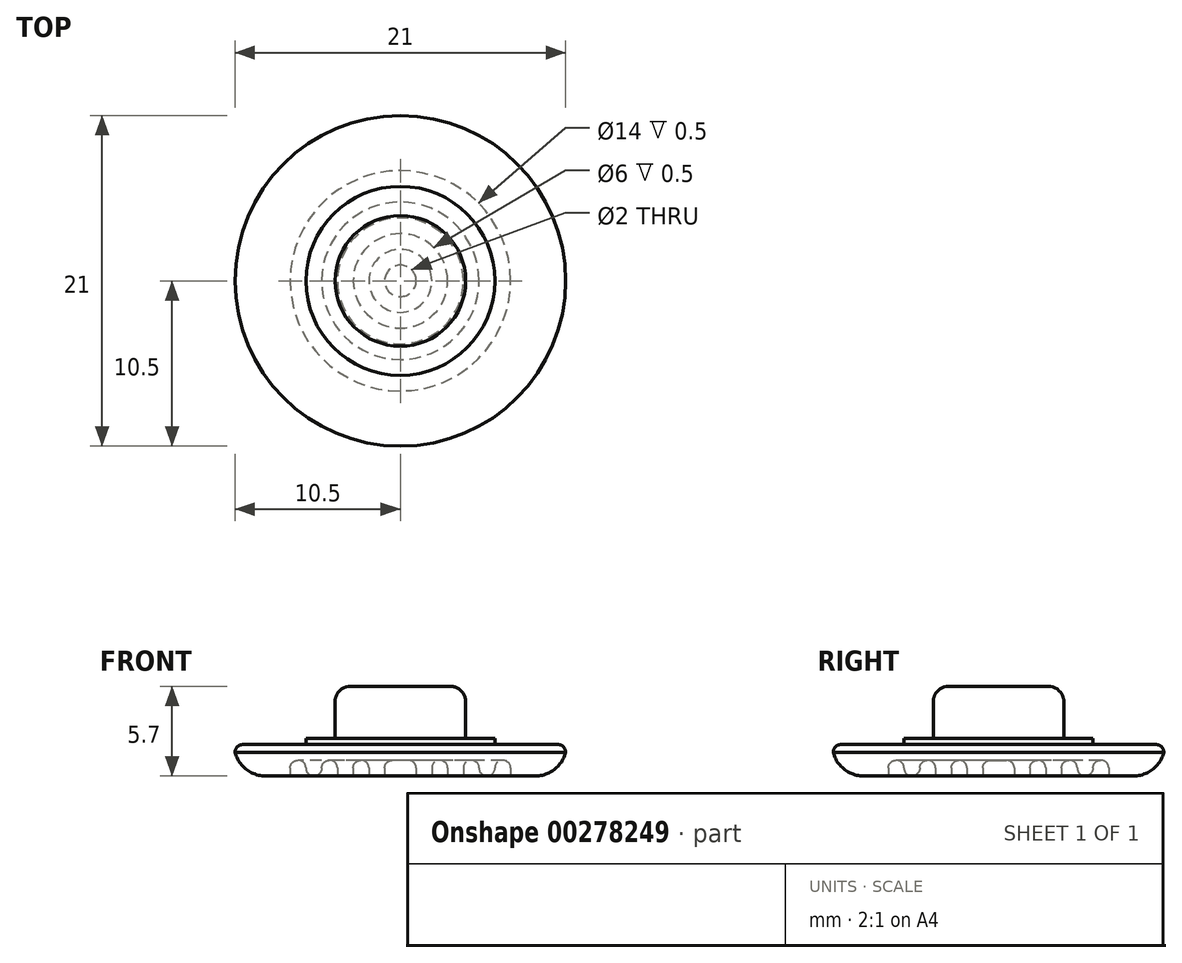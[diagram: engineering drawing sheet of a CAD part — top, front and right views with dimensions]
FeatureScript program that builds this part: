
annotation { "Feature Type Name" : "Feature", "Feature Type Description" : "" }
export const myFeature = defineFeature(function(context is Context, id is Id, definition is map)
    precondition{}
    {
        {
            var Q0;
            Q0=qCreatedBy(makeId("Top.planeOp"),FACE);
            var sketch = newSketch(context, id + "F0", { "sketchPlane" : qUnion([Q0])});
            skCircle(sketch, "E0", {"center": v(27.79, 0.83) * mm, "radius": 4.15 * mm});
            skCircle(sketch, "E1", {"center": v(27.79, 0.83) * mm, "radius": 11 * mm});
            skCircle(sketch, "E2", {"center": v(27.79, 0.83) * mm, "radius": 6 * mm});
            skCircle(sketch, "E3", {"center": v(0, 0) * mm, "radius": 4.15 * mm});
            skCircle(sketch, "E4", {"center": v(0, 0) * mm, "radius": 6 * mm});
            skCircle(sketch, "E5", {"center": v(0, 0) * mm, "radius": 10.5 * mm});
            skSolve(sketch);
        }
        {
            var Q0;
            Q0=makeQuery(id+"F0.imprint","IMPRINT",FACE,{"disambiguationData":[TD([[makeQuery(id+"F0.imprint","IMPRINT",EDGE,{"derivedFrom":sQuery(id+"F0.wireOp",EDGE,"E4")}),-1.0]])]});
            extrude(context, id + "F1", {"entities" : qUnion([Q0]), "depth" : 2 * mm, "offsetDistance" : 25 * mm});
        }
        {
            var Q0;
            Q0=makeQuery(id+"F0.imprint","IMPRINT",FACE,{"disambiguationData":[TD([[makeQuery(id+"F0.imprint","IMPRINT",EDGE,{"derivedFrom":sQuery(id+"F0.wireOp",EDGE,"E3")}),-1.0]])]});
            extrude(context, id + "F2", {"entities" : qUnion([Q0]), "operationType" : NewBodyOperationType.ADD, "depth" : 2.4 * mm, "offsetDistance" : 25 * mm});
        }
        {
            var Q0;
            Q0=makeQuery(id+"F0.imprint","IMPRINT",FACE,{"disambiguationData":[TD([[makeQuery(id+"F0.imprint","IMPRINT",EDGE,{"derivedFrom":sQuery(id+"F0.wireOp",EDGE,"E3")}),1.0]])]});
            extrude(context, id + "F3", {"entities" : qUnion([Q0]), "operationType" : NewBodyOperationType.ADD, "depth" : 5.7 * mm, "offsetDistance" : 25 * mm});
        }
        {
            var Q0;
            Q0=makeQuery(id+"F3.opExtrude","CAP_EDGE",EDGE,{"disambiguationData":[OSD([sQuery(id+"F0.wireOp",EDGE,"E3")])],"isStart":false});
            fillet(context, id + "F4", {"entities" : qUnion([Q0]), "radius" : 1 * mm, "tangentPropagation" : true, "allowEdgeOverflow" : false});
        }
        {
            var Q0;
            Q0=makeQuery(id+"F1.opExtrude","CAP_EDGE",EDGE,{"disambiguationData":[OSD([sQuery(id+"F0.wireOp",EDGE,"E5")])],"isStart":false});
            fillet(context, id + "F5", {"entities" : qUnion([Q0]), "radius" : .5 * mm, "tangentPropagation" : true, "allowEdgeOverflow" : false});
        }
        {
            var Q0;
            Q0=makeQuery(id+"F1.opExtrude","CAP_EDGE",EDGE,{"disambiguationData":[OSD([sQuery(id+"F0.wireOp",EDGE,"E5")])],"isStart":true});
            fillet(context, id + "F6", {"entities" : qUnion([Q0]), "radius" : 2 * mm, "tangentPropagation" : true, "allowEdgeOverflow" : false});
        }
        {
            var Q0;
            Q0=makeQuery(id+"F0.imprint","IMPRINT",FACE,{"disambiguationData":[TD([[makeQuery(id+"F0.imprint","IMPRINT",EDGE,{"derivedFrom":sQuery(id+"F0.wireOp",EDGE,"E3")}),1.0]])]});
            var sketch = newSketch(context, id + "F7", { "sketchPlane" : qUnion([Q0])});
            skCircle(sketch, "E6", {"center": v(0, 0) * mm, "radius": 11 * mm});
            skCircle(sketch, "E7", {"center": v(0, 0) * mm, "radius": 8 * mm});
            skCircle(sketch, "E8", {"center": v(0, 0) * mm, "radius": 7.5 * mm});
            skCircle(sketch, "E9", {"center": v(0, 0) * mm, "radius": 7 * mm});
            skCircle(sketch, "E10", {"center": v(0, 0) * mm, "radius": 6 * mm});
            skCircle(sketch, "E11", {"center": v(0, 0) * mm, "radius": 5.5 * mm});
            skCircle(sketch, "E12", {"center": v(0, 0) * mm, "radius": 5 * mm});
            skCircle(sketch, "E13", {"center": v(0, 0) * mm, "radius": 4.5 * mm});
            skCircle(sketch, "E14", {"center": v(0, 0) * mm, "radius": 4 * mm});
            skCircle(sketch, "E15", {"center": v(0, 0) * mm, "radius": 3.5 * mm});
            skCircle(sketch, "E16", {"center": v(0, 0) * mm, "radius": 3 * mm});
            skCircle(sketch, "E17", {"center": v(0, 0) * mm, "radius": 2.5 * mm});
            skCircle(sketch, "E18", {"center": v(0, 0) * mm, "radius": 2 * mm});
            skCircle(sketch, "E19", {"center": v(0, 0) * mm, "radius": 1.5 * mm});
            skCircle(sketch, "E20", {"center": v(0, 0) * mm, "radius": 1 * mm});
            skCircle(sketch, "E21", {"center": v(0, 0) * mm, "radius": 0.5 * mm});
            skCircle(sketch, "E22", {"center": v(0, 0) * mm, "radius": 6.5 * mm});
            skCircle(sketch, "E23", {"center": v(0, 0) * mm, "radius": 8.5 * mm});
            skCircle(sketch, "E24", {"center": v(0, 0) * mm, "radius": 9 * mm});
            skSolve(sketch);
        }
        {
            var Q0;
            Q0=makeQuery(id+"F7.imprint","IMPRINT",FACE,{"disambiguationData":[TD([[makeQuery(id+"F7.imprint","IMPRINT",EDGE,{"derivedFrom":sQuery(id+"F7.wireOp",EDGE,"E21")}),1.0]])]});
            var Q1;
            Q1=makeQuery(id+"F7.imprint","IMPRINT",FACE,{"disambiguationData":[TD([[makeQuery(id+"F7.imprint","IMPRINT",EDGE,{"derivedFrom":sQuery(id+"F7.wireOp",EDGE,"E20")}),1.0]])]});
            var Q2;
            Q2=makeQuery(id+"F7.imprint","IMPRINT",FACE,{"disambiguationData":[TD([[makeQuery(id+"F7.imprint","IMPRINT",EDGE,{"derivedFrom":sQuery(id+"F7.wireOp",EDGE,"E17")}),1.0]])]});
            var Q3;
            Q3=makeQuery(id+"F7.imprint","IMPRINT",FACE,{"disambiguationData":[TD([[makeQuery(id+"F7.imprint","IMPRINT",EDGE,{"derivedFrom":sQuery(id+"F7.wireOp",EDGE,"E16")}),1.0]])]});
            var Q4;
            Q4=makeQuery(id+"F7.imprint","IMPRINT",FACE,{"disambiguationData":[TD([[makeQuery(id+"F7.imprint","IMPRINT",EDGE,{"derivedFrom":sQuery(id+"F7.wireOp",EDGE,"E13")}),1.0]])]});
            var Q5;
            Q5=makeQuery(id+"F7.imprint","IMPRINT",FACE,{"disambiguationData":[TD([[makeQuery(id+"F7.imprint","IMPRINT",EDGE,{"derivedFrom":sQuery(id+"F7.wireOp",EDGE,"E14")}),-1.0]])]});
            var Q6;
            Q6=makeQuery(id+"F7.imprint","IMPRINT",FACE,{"disambiguationData":[TD([[makeQuery(id+"F7.imprint","IMPRINT",EDGE,{"derivedFrom":sQuery(id+"F7.wireOp",EDGE,"E12")}),1.0]])]});
            var Q7;
            Q7=makeQuery(id+"F7.imprint","IMPRINT",FACE,{"disambiguationData":[TD([[makeQuery(id+"F7.imprint","IMPRINT",EDGE,{"derivedFrom":sQuery(id+"F7.wireOp",EDGE,"E10")}),-1.0]])]});
            var Q8;
            Q8=makeQuery(id+"F7.imprint","IMPRINT",FACE,{"disambiguationData":[TD([[makeQuery(id+"F7.imprint","IMPRINT",EDGE,{"derivedFrom":sQuery(id+"F7.wireOp",EDGE,"E9")}),1.0]])]});
            extrude(context, id + "F8", {"entities" : qUnion([Q0, Q1, Q2, Q3, Q4, Q5, Q6, Q7, Q8]), "operationType" : NewBodyOperationType.REMOVE, "depth" : 1 * mm, "offsetDistance" : 25 * mm});
        }
        {
            var Q0;
            Q0=makeQuery(id+"F8.boolean.opBoolean","COPY",EDGE,{"derivedFrom":makeQuery(id+"F8.opExtrude","CAP_EDGE",EDGE,{"disambiguationData":[OSD([sQuery(id+"F7.wireOp",EDGE,"E20")])],"isStart":true})});
            var Q1;
            Q1=makeQuery(id+"F8.boolean.opBoolean","COPY",EDGE,{"derivedFrom":makeQuery(id+"F8.opExtrude","CAP_EDGE",EDGE,{"disambiguationData":[OSD([sQuery(id+"F7.wireOp",EDGE,"E18")])],"isStart":true})});
            var Q2;
            Q2=makeQuery(id+"F8.boolean.opBoolean","COPY",EDGE,{"derivedFrom":makeQuery(id+"F8.opExtrude","CAP_EDGE",EDGE,{"disambiguationData":[OSD([sQuery(id+"F7.wireOp",EDGE,"E16")])],"isStart":true})});
            var Q3;
            Q3=makeQuery(id+"F8.boolean.opBoolean","COPY",EDGE,{"derivedFrom":makeQuery(id+"F8.opExtrude","CAP_EDGE",EDGE,{"disambiguationData":[OSD([sQuery(id+"F7.wireOp",EDGE,"E14")])],"isStart":true})});
            var Q4;
            {var subQ0=sQuery(id+"F0.wireOp",EDGE,"E3");var subQ1=sQuery(id+"F0.wireOp",EDGE,"E4");Q4=makeQuery(id+"F8.boolean.opBoolean","SPLIT",FACE,{"disambiguationData":[TD([makeQuery(id+"F8.opExtrude","SWEPT_FACE",FACE,{"disambiguationData":[OSD([sQuery(id+"F7.wireOp",EDGE,"E12")])]})])],"derivedFrom":makeQuery(id+"F3.boolean.opBoolean","MERGE",FACE,{"derivedFrom":[makeQuery(id+"F2.boolean.opBoolean","MERGE",FACE,{"derivedFrom":[makeQuery(id+"F1.opExtrude","CAP_FACE",FACE,{"disambiguationData":[OSD([subQ1,sQuery(id+"F0.wireOp",EDGE,"E5")])],"isStart":true}),makeQuery(id+"F2.opExtrude","CAP_FACE",FACE,{"disambiguationData":[OSD([subQ0,subQ1])],"isStart":true})]}),makeQuery(id+"F3.opExtrude","CAP_FACE",FACE,{"disambiguationData":[OSD([subQ0])],"isStart":true})]})});}
            var Q5;
            Q5=makeQuery(id+"F8.boolean.opBoolean","COPY",EDGE,{"derivedFrom":makeQuery(id+"F8.opExtrude","CAP_EDGE",EDGE,{"disambiguationData":[OSD([sQuery(id+"F7.wireOp",EDGE,"E9")])],"isStart":true})});
            fillet(context, id + "F9", {"entities" : qUnion([Q0, Q1, Q2, Q3, Q4, Q5]), "radius" : .5 * mm, "tangentPropagation" : true, "allowEdgeOverflow" : false});
        }
        {
            var Q0;
            Q0=makeQuery(id+"F8.boolean.opBoolean","COPY",FACE,{"derivedFrom":makeQuery(id+"F8.opExtrude","CAP_FACE",FACE,{"disambiguationData":[OSD([sQuery(id+"F7.wireOp",EDGE,"E9"),sQuery(id+"F7.wireOp",EDGE,"E10")])],"isStart":false})});
            var Q1;
            Q1=makeQuery(id+"F8.boolean.opBoolean","COPY",FACE,{"derivedFrom":makeQuery(id+"F8.opExtrude","CAP_FACE",FACE,{"disambiguationData":[OSD([sQuery(id+"F7.wireOp",EDGE,"E12"),sQuery(id+"F7.wireOp",EDGE,"E14")])],"isStart":false})});
            var Q2;
            Q2=makeQuery(id+"F8.boolean.opBoolean","COPY",FACE,{"derivedFrom":makeQuery(id+"F8.opExtrude","CAP_FACE",FACE,{"disambiguationData":[OSD([sQuery(id+"F7.wireOp",EDGE,"E16"),sQuery(id+"F7.wireOp",EDGE,"E18")])],"isStart":false})});
            var Q3;
            Q3=makeQuery(id+"F8.boolean.opBoolean","COPY",FACE,{"derivedFrom":makeQuery(id+"F8.opExtrude","CAP_FACE",FACE,{"disambiguationData":[OSD([sQuery(id+"F7.wireOp",EDGE,"E20")])],"isStart":false})});
            fillet(context, id + "F10", {"entities" : qUnion([Q0, Q1, Q2, Q3]), "radius" : .5 * mm, "tangentPropagation" : true, "allowEdgeOverflow" : false});
        }
    });
